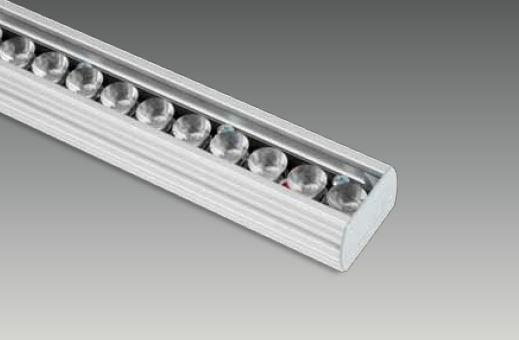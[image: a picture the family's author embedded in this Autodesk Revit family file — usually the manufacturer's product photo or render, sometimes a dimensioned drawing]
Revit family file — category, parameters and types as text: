
# Revit family: SD 0300 DMD
name_source: partatom
category: Lighting Fixtures
revit_build: Autodesk Revit 2017 (Build: 20160225_1515(x64)
units: mm (PartAtom-declared; Revit-internal decimal feet)

## family parameters
Cut with Voids When Loaded = No
Host = Face
Light Source = Yes
Part Type = Normal
Room Calculation Point = No
Round Connector Dimension = Use Diameter
Shared = No

## types (2) — shared parameters
Apparent Load = 15 VA
Beam Angle 1 = 9.00°
Beam Angle 2 = 55.00°
Color Filter = 16777215
Default Elevation = 1219 mm
Dimming Lamp Color Temperature Shift = <None>
Emit Shape Visible in Rendering = Yes
Emit from Rectangle Length = 30 mm  [stored 0.0984252 ft]
Emit from Rectangle Width = 300 mm
Light Source Symbol Size = 610 mm
Manufacturer = ARLIGHT
Type Image = SD 0300 DMD.JPG
Wattage Comments = 15W

## type names (no varying parameters)
- SDDMD.300.15.30.55
- SDDMD.300.15.40.55

note: [stored X ft] marks values corroborated as IEEE doubles in the binary element streams (Revit-internal decimal feet)

## geometry (parser evidence)
native form markers: Sweep x3
no freeform markers — native parametric forms only
